# Revit family: WCSeatCover-Duroplast-TopFixing-SoftClosing-Vitra-S20Series_77-003-009
name_source: partatom
category: Plumbing Fixtures
revit_build: Autodesk Revit 2017 (Build: 20160225_1515(x64)
units: mm (PartAtom-declared; Revit-internal decimal feet)

## family parameters
Cut with Voids When Loaded = No
Host = Face
OmniClass Number = 23.45.05.21
OmniClass Title = Plumbing Fixtures - Sanitary Disposal Units
Part Type = Normal
Room Calculation Point = No
Round Connector Dimension = Use Diameter
Shared = Yes

## types (3) — shared parameters
BIMobject category = Sanitary - Toilet Seats
CW Connection = No
Color = White
Default Elevation = 410 mm  [stored 1.34514 ft]
Description = VitrA S20 WC Seat
Design country = Turkey
HW Connection = No
IFC Classification = Sanitary Terminal
Manufacturer = Vitra
Manufacturer name = Vitra
NBS Referans Code = 35-93-95
NBS Referans Description = Wc Seats And Covers
Nominal Depth (mm) = 440 mm  [stored 1.44357 ft]
Nominal Height (mm) = 60 mm
Nominal Width (mm) = 360 mm  [stored 1.1811 ft]
OmniClass Code = 23-31 19 19 11
OmniClass Description = Toilets
Product certification = https://vitraglobal.com
Product family = S20
Secondary Material = White
Technical description = https://www.vitra.com.tr
UNSPSC Code = 35-93-95
UNSPSC Description = Water Operated Water Closets
URL = https://www.vitra.com.tr
Uniclass 1.4 Code = L72164
Uniclass 1.4 Description = Toilets
Uniclass 2.0 Code = PR-35-93-95
Uniclass 2.0 Description = Wc Seats And Covers
Uniclass 2015 Code = Pr_40_20_93_95
Uniclass 2015 Name = WC seats and covers
Vent Connection = No
Warranty Period (Year) = 2 Years
Waste Connection = No
Weight Net (kg) = 2,83
Youtube = https://www.youtube.com
zero-valued in all types: Cost

## per-type parameters (varying)
| type | Article No. (default) | Main Material | Model | Product SKU | Product data url | Product url |
| WCSeat_Vitra_S20_77-003-009 | 77-003-009 | Plastic | 77-003-009 | 77-003-009 |  | https://www.vitra.com.tr |
| WCSeat_Vitra_S20_77-003-001 | 77-003-001 | Ceramic | 77-003-001 | 77-003-001 | https://www.vitra.com.tr |  |
| WCSeat_Vitra_S20_77-003R009 | 77-003R009 | Ceramic | 77-003R009 | 77-003R009 | https://www.vitra.com.tr |  |

note: [stored X ft] marks values corroborated as IEEE doubles in the binary element streams (Revit-internal decimal feet)

## geometry (parser evidence)
native form markers: Sweep x3
no freeform markers — native parametric forms only
